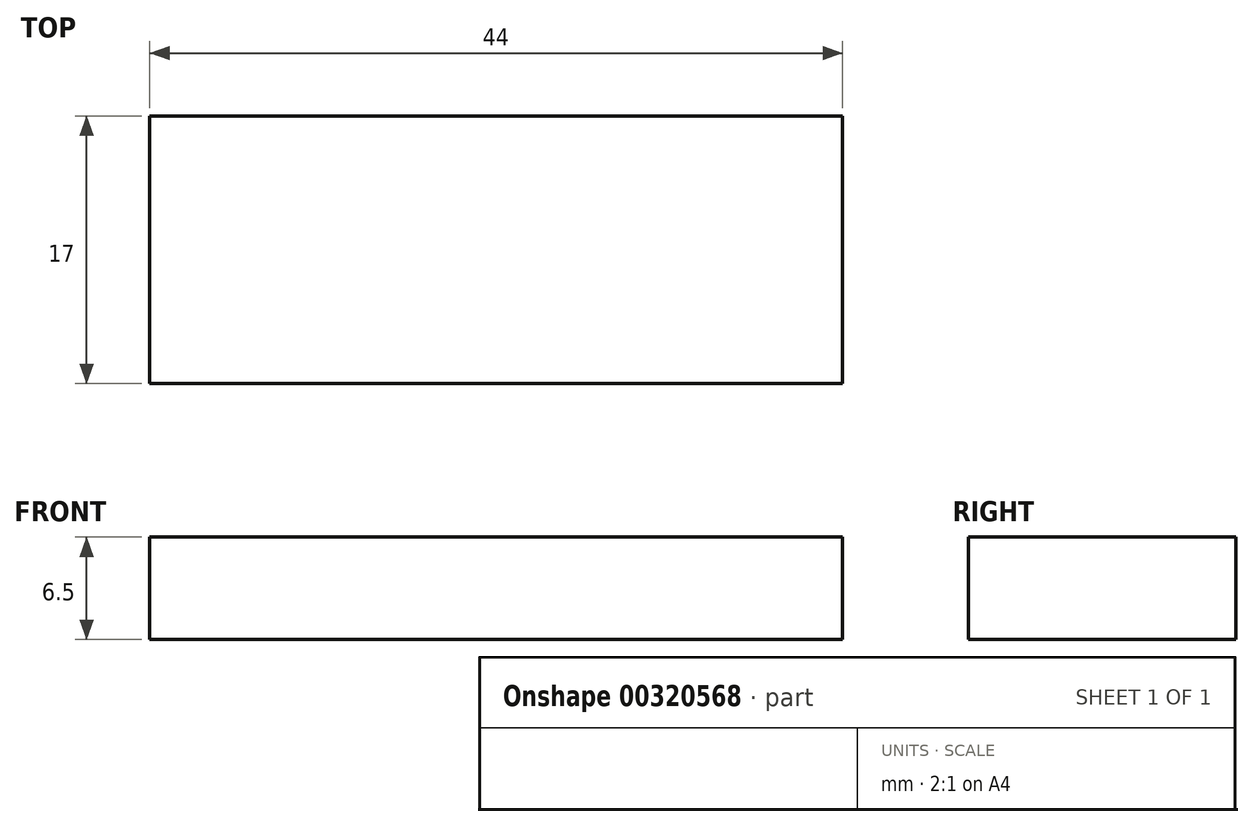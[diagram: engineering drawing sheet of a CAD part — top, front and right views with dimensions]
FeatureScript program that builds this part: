
annotation { "Feature Type Name" : "Feature", "Feature Type Description" : "" }
export const myFeature = defineFeature(function(context is Context, id is Id, definition is map)
    precondition{}
    {
        {
            var Q0;
            Q0=qCreatedBy(makeId("Top.planeOp"),FACE);
            var sketch = newSketch(context, id + "F0", { "sketchPlane" : qUnion([Q0])});
            skLineSegment(sketch, "E0.bottom", {"start": v(0, 0) * mm, "end": v(44, 0) * mm});
            skLineSegment(sketch, "E0.top", {"start": v(0, 17) * mm, "end": v(44, 17) * mm});
            skLineSegment(sketch, "E0.left", {"start": v(0, 0) * mm, "end": v(0, 17) * mm});
            skLineSegment(sketch, "E0.right", {"start": v(44, 0) * mm, "end": v(44, 17) * mm});
            skSolve(sketch);
        }
        {
            var Q0;
            Q0=makeQuery(id+"F0.imprint","IMPRINT",FACE,{"disambiguationData":[TD([[makeQuery(id+"F0.imprint","IMPRINT",EDGE,{"derivedFrom":sQuery(id+"F0.wireOp",EDGE,"E0.bottom")}),1.0]])]});
            extrude(context, id + "F1", {"entities" : qUnion([Q0]), "depth" : 6.5 * mm});
        }
    });
